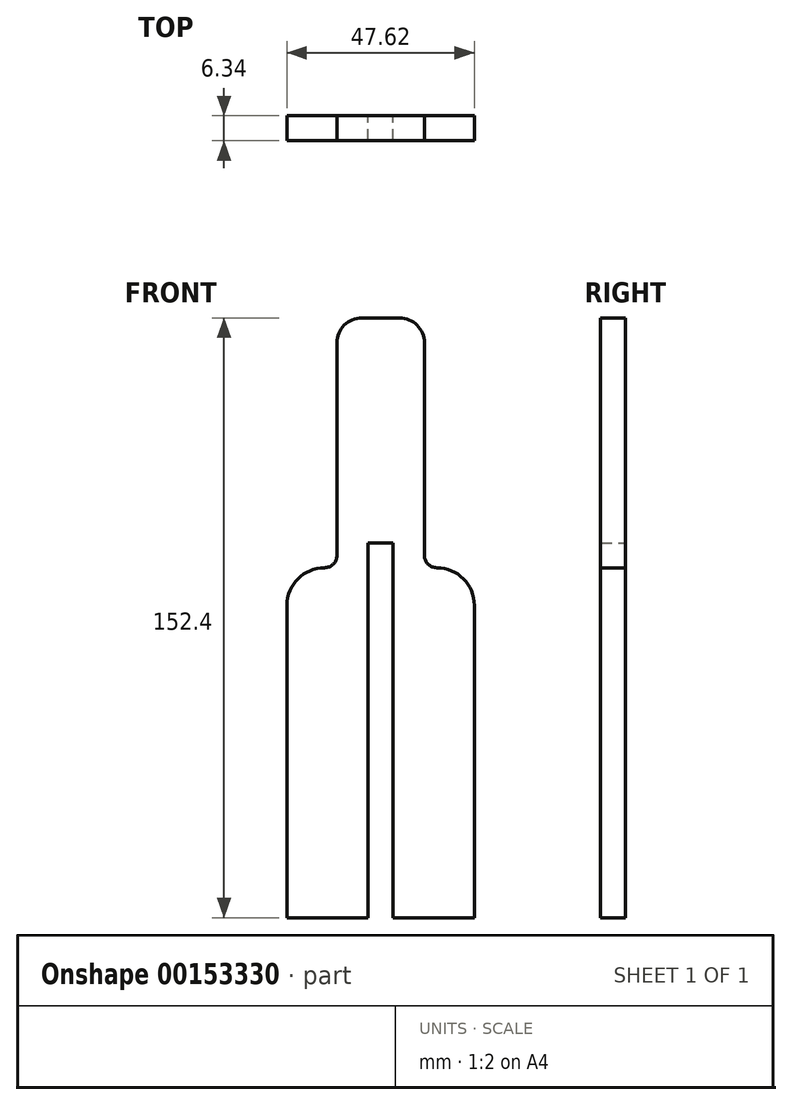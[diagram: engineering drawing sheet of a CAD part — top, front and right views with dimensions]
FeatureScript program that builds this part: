
annotation { "Feature Type Name" : "Feature", "Feature Type Description" : "" }
export const myFeature = defineFeature(function(context is Context, id is Id, definition is map)
    precondition{}
    {
        {
            var Q0;
            Q0=qCreatedBy(makeId("Front.planeOp"),FACE);
            var sketch = newSketch(context, id + "F0", { "sketchPlane" : qUnion([Q0])});
            skLineSegment(sketch, "E0.bottom", {"start": v(-4.76, 107.95) * mm, "end": v(4.76, 107.95) * mm});
            skLineSegment(sketch, "E0.left", {"start": v(-11.11, 101.6) * mm, "end": v(-11.11, 47.62) * mm});
            skLineSegment(sketch, "E0.right", {"start": v(11.11, 101.6) * mm, "end": v(11.11, 47.62) * mm});
            skLineSegment(sketch, "E1.bottom", {"start": v(-14.29, 44.45) * mm, "end": v(-14.29, 44.45) * mm});
            skLineSegment(sketch, "E1.top", {"start": v(-23.81, -44.45) * mm, "end": v(-3.18, -44.45) * mm});
            skLineSegment(sketch, "E1.left", {"start": v(-23.81, 34.93) * mm, "end": v(-23.81, -44.45) * mm});
            skLineSegment(sketch, "E1.right", {"start": v(23.81, 34.93) * mm, "end": v(23.81, -44.45) * mm});
            skLineSegment(sketch, "E2.trimOffspring", {"start": v(14.29, 44.45) * mm, "end": v(14.29, 44.45) * mm});
            skPoint(sketch, "E3.visualSharp", {"position": v(-11.11, 44.45) * mm});
            skArc(sketch, "E3.filletArc", {"start": v(-14.29, 44.45) * mm, "mid": v(-12.04, 45.38) * mm, "end": v(-11.11, 47.62) * mm});
            skPoint(sketch, "E4.visualSharp", {"position": v(11.11, 44.45) * mm});
            skArc(sketch, "E4.filletArc", {"start": v(11.11, 47.62) * mm, "mid": v(12.04, 45.38) * mm, "end": v(14.29, 44.45) * mm});
            skPoint(sketch, "E5.visualSharp", {"position": v(-11.11, 107.95) * mm});
            skArc(sketch, "E5.filletArc", {"start": v(-4.76, 107.95) * mm, "mid": v(-9.25, 106.1) * mm, "end": v(-11.11, 101.6) * mm});
            skPoint(sketch, "E6.visualSharp", {"position": v(11.11, 107.95) * mm});
            skArc(sketch, "E6.filletArc", {"start": v(11.11, 101.6) * mm, "mid": v(9.25, 106.1) * mm, "end": v(4.76, 107.95) * mm});
            skPoint(sketch, "E7.visualSharp", {"position": v(-23.81, 44.45) * mm});
            skArc(sketch, "E7.filletArc", {"start": v(-14.29, 44.45) * mm, "mid": v(-21.02, 41.66) * mm, "end": v(-23.81, 34.93) * mm});
            skPoint(sketch, "E8.visualSharp", {"position": v(23.81, 44.45) * mm});
            skArc(sketch, "E8.filletArc", {"start": v(23.81, 34.93) * mm, "mid": v(21.02, 41.66) * mm, "end": v(14.29, 44.45) * mm});
            skLineSegment(sketch, "E9.bottom", {"start": v(3.18, 50.8) * mm, "end": v(-3.18, 50.8) * mm});
            skLineSegment(sketch, "E9.left", {"start": v(3.18, 50.8) * mm, "end": v(3.18, -44.45) * mm});
            skLineSegment(sketch, "E9.right", {"start": v(-3.18, 50.8) * mm, "end": v(-3.18, -44.45) * mm});
            skPoint(sketch, "E9.middle", {"position": v(0, 0) * mm});
            skLineSegment(sketch, "E10.trimOffspring", {"start": v(3.18, -44.45) * mm, "end": v(23.81, -44.45) * mm});
            skSolve(sketch);
        }
        {
            var Q0;
            Q0 = qSketchRegion(id + "F0", true);
            extrude(context, id + "F1", {"entities" : qUnion([Q0]), "endBound" : BoundingType.SYMMETRIC, "depth" : 6.35 * mm});
        }
    });
